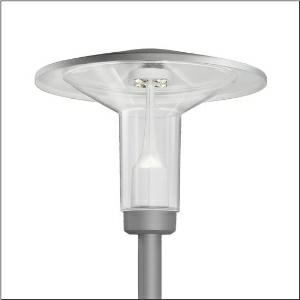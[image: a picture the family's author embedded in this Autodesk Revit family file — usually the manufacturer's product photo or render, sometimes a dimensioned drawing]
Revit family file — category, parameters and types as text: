
# Revit family: laterne_iq___st1_2a_5xa5255mf14h_e85f
name_source: partatom
category: Lighting Fixtures
units: mm (PartAtom-declared; Revit-internal decimal feet)

## family parameters
Cut with Voids When Loaded = No
Host = Face
Light Source = No
Part Type = Normal
Room Calculation Point = No
Round Connector Dimension = Use Diameter
Shared = No

## types (1)
- --- (1 x LED, 1540 lm, 11.8 W, 2700K)
    Apparent Load = 12 VA
    CIE Flux Codes = 25 63 94 98 100
    Color Rendering = 70
    Color Temperature = 2700K
    Default Elevation = 1800 mm
    Description = Lantern iQ, mast luminaire, Module 540 iQ-SR, primary light control with 3 zone facetted reflector, of plastic, silver coated, highly specular, structured, primary optical cover: cover, of PMMA, transparent, light distribution: ST1.2a, light emission: direct distribution, primary light characteristic: asymmetric, installation type: post-top, LED, High Power LED, rated luminous flux: 1.540lm, luminous efficacy: 131lm/W, light colour: 727, colour temperature: 2700K, control gear: iQ Street-Remote, control: pre-setting: logarithmic dimming characteristic, Street-Remote, Auto-Match, Temp-Guard, Lumen-Switch, Night-Set, Smart-Wire, Light-Fading, Desk-Remote (wireless, voltage-free reading and setting of iQ features in the workshop via application-optimized NFC function/RFID function), optimised constant luminous flux control (CLO 2.0), with terminal, 6-pole, max. 2.5mm², mains connection: 230..240V, AC, 50/60Hz, start of lifetime: 12W, end of service life: 12W, reduction: 6W, luminaire housing, upper part, of glass-fibre reinforced polyester, coated, Siteco® metallic grey (DB 702S), diameter: 750mm, height: 583mm, spigot size: d x l = 76 x 70mm (post-top) | with reducer (optional accessory) 60 x 70mm, mounting height: 3..5m, post-top mast mounting element, of diecast aluminium, coated, Siteco® metallic grey (DB 702S), Module 540 iQ-SR, traffic white (RAL 9016), equipment: standard, protection rating (complete): IP65, insulation class (complete): insulation class II (safety insulation), certification: CE, ENEC, VDE, packaging unit: 1 piece

Light Distribution: ST1.2a
    Height = 583 mm
    Lamp = 1 x LED
    Lamp Light Flux = 1540 lm
    Lamp Power = 11.8 W
    Lamp count = 1
    Length = 750 mm
    Luminous efficacy = 131 lm/W
    Manufacturer = Siteco
    ModVariant = No
    Model = 5XA5255MF14H
    Number of Poles = 1
    OnlyDefault = Yes
    Power Factor = 1
    Product Name = Laterne iQ | ST1.2a
    Product group = mast luminaire | pylon top
    ProductGroupID = 6100
    Protection Class = Protection class II
    Protection Degree = IP 65
    RLX_Detail_Level = 1
    RLX_Emergency_Light_Flux = 0 lm
    RLX_Emergency_Type = 0
    RLX_Emergency_Type_DB = No
    RlxData = <blob elided: 90025 chars, md5=caf10316>
    Socket = socket
    Standby Power = 0 W
    System Light Flux = 1540 lm
    System Power = 12 W
    Type Comments = factory setting: luminous flux: 100 % | dim-lin: 254 | 472 mA
    Type Image = l_1006050.jpg
    URL = http://relux.com
    VarID = @adj_174887
    Voltage = 0 V
    Weight = 0.00 kg
    Width = 0 mm  [stored 0 ft]

note: [stored X ft] marks values corroborated as IEEE doubles in the binary element streams (Revit-internal decimal feet)

## geometry (parser evidence)
native form markers: Blend x4, Sweep x12
no freeform markers — native parametric forms only
